# Revit family: Vitra-Sento-Tall Unit-60860-60861-60862-60848-60849-60850
name_source: partatom
category: Furniture Systems
units: mm (PartAtom-declared; Revit-internal decimal feet)

## family parameters
Cut with Voids When Loaded = No
Host = Face
OmniClass Number = 23.40.00.00
OmniClass Title = Equipment and Furnishings
Part Type = Normal
Room Calculation Point = No
Round Connector Dimension = Use Diameter
Shared = Yes

## types (6) — shared parameters
BIMobject category = Storage
Construction Type = Wall Mounted
Default Elevation = 1170 mm  [stored 3.83858 ft]
Depth = 350 mm  [stored 1.14829 ft]
Description = Sento Tall Unit, 40 cm, without legs
Design country = Turkey
Height = 1575 mm  [stored 5.16732 ft]
IFC Classification = Furniture
Manufacturer = Vitra
Manufacturer name = Vitra
Masterformat 2014 Code = 12 35 30.23
Masterformat 2014 Description = Bathroom Casework
NBS Reference Code = 35-75-08
NBS Reference Description = Bathroom Cabinets
OmniClass Code = 23-31 25 13
OmniClass Description = Bathroom Cabinets
Product certification = https://vitraglobal.com
Product data url = https://www.vitraglobal.com
Product family = Sento
Product group = Bathroom Furniture
Secondary Material = Vitra-Light Oak
Technical description = https://www.vitraglobal.com
UNSPSC Code = 30161801
UNSPSC Description = Bathroom Cabinets
URL = https://vitraglobal.com
Uniclass 1.4 Code = L8241
Uniclass 1.4 Description = Bathroom Cabinets
Uniclass 2.0 Code = PR-35-75-08
Uniclass 2.0 Description = Bathroom Cabinets
Uniclass 2015 Code = Pr_40_30_78_03
Uniclass 2015 Name = Bathroom Cabinets
Uniformat II Code = E2010
Uniformat II Description = Fixed Furnishings
Warranty Period (Year) = 2
Width = 400 mm  [stored 1.31234 ft]
Youtube = https://www.youtube.com
zero-valued in all types: Nominal height, Nominal width

## per-type parameters (varying)
| type | Model | Primary Material | Product SKU | Weight Net (kg) |
| Vitra_Sento Tall Unit, 40 cm, without legs, Matte White, left_60860 | 60860 | Vitra-MattWhite | 60860 | 50,500 |
| Vitra_Sento Tall Unit, 40 cm, without legs, Matte Cream, left_60861 | 60861 | Vitra-Metal | 60861 | 53,000 |
| Vitra_Sento Tall Unit, 40 cm, without legs, Matte Anthracite, left_60862 | 60862 | Vitra-DarkOlive | 60862 | 53,000 |
| Vitra_Sento Tall Unit, 40 cm, without legs, Matte White, right_60848 | 60848 | Vitra-MattWhite | 60848 | 53,000 |
| Vitra_Sento Tall Unit, 40 cm, without legs, Matte Cream, right_60849 | 60849 | Vitra-Metal | 60849 | 53,000 |
| Vitra_Sento Tall Unit, 40 cm, without legs, Matte Anthracite, right_60850 | 60850 | Vitra-DarkOlive | 60850 | 53,000 |

note: [stored X ft] marks values corroborated as IEEE doubles in the binary element streams (Revit-internal decimal feet)

## geometry (parser evidence)
native form markers: Sweep x3
no freeform markers — native parametric forms only
